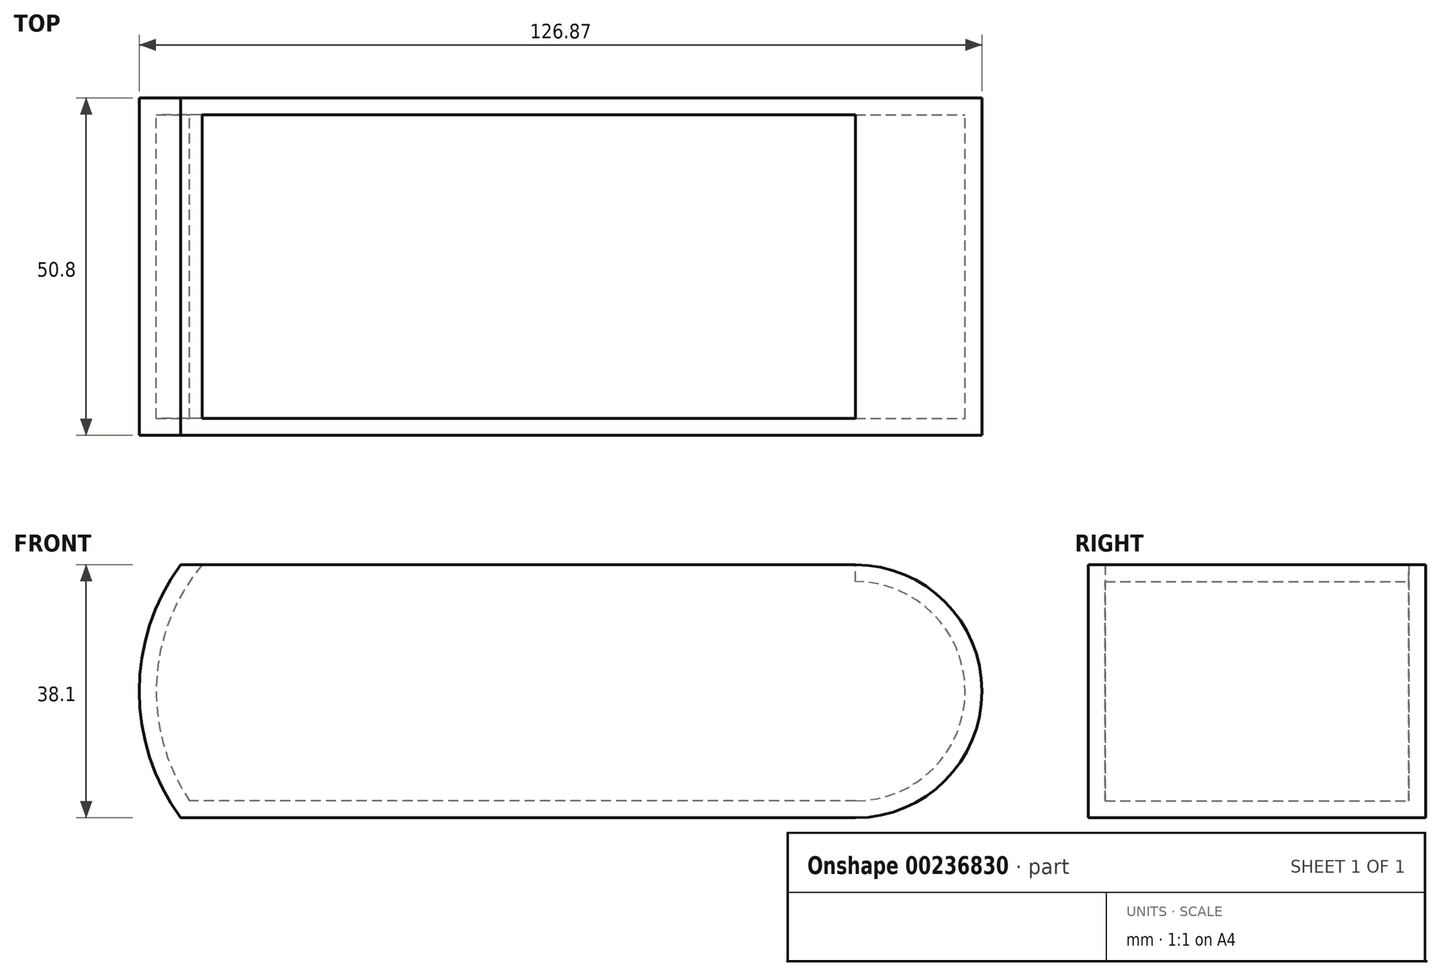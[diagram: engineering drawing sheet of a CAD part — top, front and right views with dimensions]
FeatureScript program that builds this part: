
annotation { "Feature Type Name" : "Feature", "Feature Type Description" : "" }
export const myFeature = defineFeature(function(context is Context, id is Id, definition is map)
    precondition{}
    {
        {
            var Q0;
            Q0=qCreatedBy(makeId("Front.planeOp"),FACE);
            var sketch = newSketch(context, id + "F0", { "sketchPlane" : qUnion([Q0])});
            skLineSegment(sketch, "E0.bottom", {"start": v(50.8, 19.05) * mm, "end": v(-50.8, 19.05) * mm});
            skLineSegment(sketch, "E0.top", {"start": v(50.8, -19.05) * mm, "end": v(-50.8, -19.05) * mm});
            skPoint(sketch, "E0.middle", {"position": v(0, 0) * mm});
            skArc(sketch, "E1", {"start": v(-50.8, 19.05) * mm, "mid": v(-57.02, 0) * mm, "end": v(-50.8, -19.05) * mm});
            skArc(sketch, "E2", {"start": v(50.8, -19.05) * mm, "mid": v(69.85, 0) * mm, "end": v(50.8, 19.05) * mm});
            skSolve(sketch);
        }
        {
            var Q0;
            Q0=makeQuery(id+"F0.imprint","IMPRINT",FACE,{"disambiguationData":[TD([[makeQuery(id+"F0.imprint","IMPRINT",EDGE,{"derivedFrom":sQuery(id+"F0.wireOp",EDGE,"E0.bottom")}),1.0]])]});
            extrude(context, id + "F1", {"entities" : qUnion([Q0]), "endBound" : BoundingType.SYMMETRIC, "depth" : 50.8 * mm});
        }
        {
            var Q0;
            Q0=makeQuery(id+"F1.opExtrude","SWEPT_FACE",FACE,{"disambiguationData":[OSD([sQuery(id+"F0.wireOp",EDGE,"E0.bottom")])]});
            shell(context, id + "F2", {"entities" : qUnion([Q0]), "thickness" : 2.54 * mm});
        }
    });
